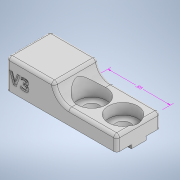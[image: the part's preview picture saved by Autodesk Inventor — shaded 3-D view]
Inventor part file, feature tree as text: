
AUTODESK INVENTOR PART (.ipt)
format: ipt  version: 2020 (Build 240168000, 168)  size: 298,496 bytes
history: native  units: in
note: dims shown in document units (in); Inventor stores cm internally (conversion verified against a paired STEP export)
features: sketch x6, extrude x4, fillet x3, other x2, hole x1, emboss x1
ambient origin geometry x8: Origin, YZ Plane, XZ Plane, XY Plane, X Axis, Y Axis, Z Axis, Center Point
bodies: Solid1 (feature_tree)
feature tree (17):
  other  "Annotations"
  extrude  "Extrusion1"  Depth=0.6in
  extrude  "Extrusion2"  Depth=0.65in
  extrude  "Extrusion3"  Depth=0.2in TaperAngle=0.0deg
  sketch  "Sketch4"  dims[d8=0.05in d9=0.2in]
  extrude  "Extrusion4"  Depth=0.2in
  hole  "Hole2"  [1 undecoded]
  fillet  "Fillet1"  [1 undecoded]
  fillet  "Fillet2"  Radius=0.2in
  fillet  "Fillet3"  Radius=0.6in
  emboss  "Emboss1"
  sketch  "Sketch1"  dims[d0=1.5in d1=0.6in]
  sketch  "Sketch2"  dims[d2=0.2in d3=0.0in d4=0.65in]
  sketch  "Sketch3"  dims[d5=0.6in d6=0.2in d7=0.0in]
  sketch  "Sketch5"  dims[d10=0.2in d11=0.4in d12=90.0deg d13=0.2in d14=0.6in d15=0.0in]
  sketch  "Sketch6"  dims[d19=0.2125in d20=0.2125in d21=180.0deg d22=0.213in d23=180.0deg d31=0.1in d32=0.2in d33=1.5in d34=0.2in d35=0.05in d36=0.0in d37=0.2in d38=0.75in d39=0.4in d40=0.15in d41=0.5635in d42=1.0in d43=0.0in d44=0.2in d45=0.04in d46=0.02in d47=0.02in d48=0.0in d16=0.1524in d17=0.1696in d18=0.85in]
  other  "Linear Dimension 1"
note: 2 required parameter values undecoded (feature->parameter linkage not recoverable at this tier; creation-order binding heuristic only, values carry confidence <= 0.55)
